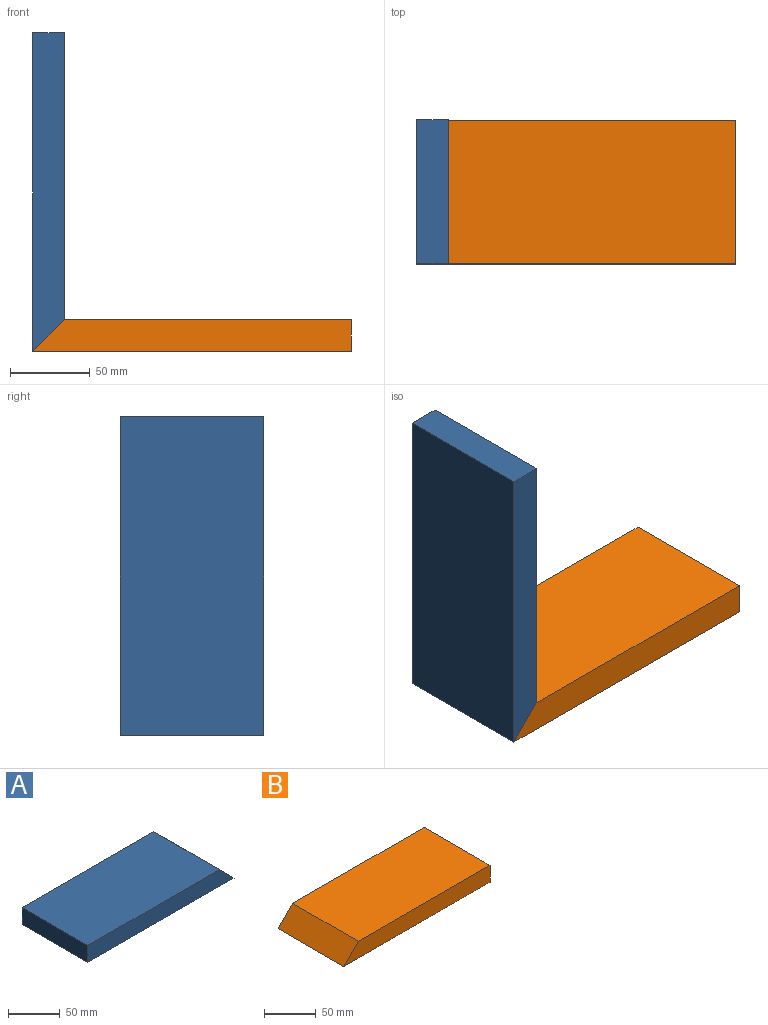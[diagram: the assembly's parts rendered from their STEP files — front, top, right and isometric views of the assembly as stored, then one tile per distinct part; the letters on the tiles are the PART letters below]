
ASSEMBLY  parts=2 mates=1
PART A: 6 faces, bbox 200x90x20 mm
  f0: plane 180x90mm, normal (0,0,1), area 16200mm2, adj f1,f3,f4,f5
  f1: plane 90x20mm, normal (-1,0,0), area 1800mm2, adj f0,f2,f3,f4
  f2: plane 200x90mm, normal (0,0,-1), area 18000mm2, adj f1,f3,f4,f5
  f3: plane 200x20mm, normal (0,-1,0), area 3800mm2, adj f0,f1,f2,f5
  f4: plane 200x20mm, normal (0,1,0), area 3800mm2, adj f0,f1,f2,f5
  f5: plane 90x20mm, normal (0.71,0,0.71), area 2545.6mm2, adj f0,f2,f3,f4
PART B: 6 faces, bbox 200x90x20 mm
  f0: plane 90x20mm, normal (1,0,0), area 1800mm2, adj f1,f2,f3,f4
  f1: plane 180x90mm, normal (0,0,1), area 16200mm2, adj f0,f3,f4,f5
  f2: plane 200x90mm, normal (0,0,-1), area 18000mm2, adj f0,f3,f4,f5
  f3: plane 200x20mm, normal (0,-1,0), area 3800mm2, adj f0,f1,f2,f5
  f4: plane 200x20mm, normal (0,1,0), area 3800mm2, adj f0,f1,f2,f5
  f5: plane 90x20mm, normal (-0.71,0,0.71), area 2545.6mm2, adj f1,f2,f3,f4
PLACE A rot(axis=(0,1,0),90deg) t=(-194.61,45,91.5)mm
PLACE B t=(-48.15,45,1.5)mm
MATE planar A.f5 <-> B.f5  axis (0.71,0,-0.71) through (-138.15,0,1.5)mm
